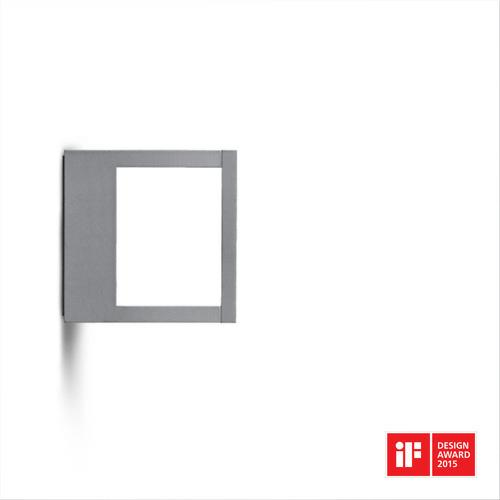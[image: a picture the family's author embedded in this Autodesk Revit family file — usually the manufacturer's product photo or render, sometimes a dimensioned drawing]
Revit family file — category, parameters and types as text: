
# Revit family: SIMES_S.7281W_Cool Square applique
name_source: partatom
category: Lighting Fixtures
revit_build: Autodesk Revit 2016 (Build: 20150714_1515(x64)
units: mm (PartAtom-declared; Revit-internal decimal feet)

## family parameters
Cut with Voids When Loaded = No
Host = Face
Light Source = Yes
OmniClass Number = 23.80.70.14
OmniClass Title = Luminaries for External Lighting
Part Type = Normal
Room Calculation Point = No
Round Connector Dimension = Use Diameter
Shared = No

## types (1)
- SIMES_S.7281W_Cool Square applique
    Approval mark = CE, ENEC
    Assembly Code = D5020
    Color Filter = 16777215
    Color Rendering Index = CRI 90
    Colour Temperature = 3000
    Control Gear = electronic transformer
    Default Elevation = 1219 mm
    Description = MINICOOL SQUARE APPLIQUE
Art. S.7281W
MODULES LED 3000K  230V CRI 90 MacAdam step 3
Rated luminaire luminous flux: 483lm
Rated input power: 12.5W
Luminaire efficacy: 39lm/W
Electronic ballast 220÷240V 0/50/60Hz
CE - ENEC 03

PRODUCT TYPE
Wall mounted luminaire or Bollard fitting ( bollard version ). IP rating IP 54
MATERIAL CHARACTERISTICS
Aluminium die cast housing in EN AB-47100 (low copper content) with high resistance against corrosion. Extruded EN AW-6060 aluminium structure (bollard version) with high corrosion resistance. Stone wash surface treatment prior to painting process. A4 grade Stainless Steel screws with 2,5-3% molybdenum content which increases the resistance against corrosion. Silicone gaskets. Painting Process : 3 Step Process
1) Surface treatment with BONDERITE. A heavy metal free chemical surface treatment containing ceramic nano particles giving a cohesive, inorganic and highly dense protective coating. 2) PRE POLYMERIZATION a process of introducing an epoxy primer with excellent characteristics to the paint which also offers very high resistance to oxidation due to its Zinc content. 3) POLYMERIZATION a process with the application of polyester powder with high resistance against UV rays and harsh weather conditions. Resistance test protection for Marine applications for 1200h.  Mechanical resistance IK 06
LIGHTING PERFORMANCE
Toughened glass diffuser. LOR --. Colour rendering index  CRI 90, Colour stability step  MacAdam step 3. 
WIRING
MICROCOOL hard wired with H07RN-F cable . MINICOOL and COOL is supplied with single cable entry.  Isolation: CLASS I . Available colours: White (cod.01), Aluminium grey (cod.14). Weight: 1.52 Kg Glow Wire test: --
Lamp included.
LOOK and COOL REGISTERED DESIGN
This luminaire contains built-in LED modules with energy class: A, A+, A++. In case of damage or malfunction please contact the manufacturer to receive additional instructions on how to replace and relative spare parts to order. The LED modules cannot be handled in the luminaire by the end user (Regulation UE 874/2012).
LED circuit boards are engineered accordingly to actual Lumen Maintenance regulation (LM80) and Technical Memorandum (TM21) where uniformity and quality of light is 50.000 hours referred to L70  B20 Ta 25°C.Lifecycle refers to LED circuit boards only, all others components of the luminaire are excluded.

EMERGENCY VERSIONS The fittings operates both on AC ( 50/60Hz ) and DC ( 0Hz ) voltage.
    Dimming Lamp Color Temperature Shift = <None>
    Frequency = 0/50/60Hz
    IFC Classification = Light Fixture
    IK Rating = IK 06
    Lamp = LED
    Lamp Light Flux = 1090
    Lamp count = 1
    Last Update = 02/08/2018 10:13:56
    Lifetime = 50000 L70 B20 Ta 25°C
    Light Output Ratio = 100
    Luminous efficacy = 38,6
    Manufacturer = SIMES
    Masterformat 2014 Code = 26 56 00
    Masterformat 2014 Description = Exterior Lighting
    Model = S.7281W
    Mounting Place = Wall
    Mounting Type = Surface mounted
    NBS Reference Code = 49
    NBS Reference Description = Luminaries And Lamps
    OmniClass Code = 23-35 47 11
    OmniClass Description = Lighting Fixture
    Photometric Web File = S7281W.ies
    Product Group = wall-mounted luminaire
    Product Name = Cool Square applique
    Protection Class = Protection class I
    Protection Degree = IP 54
    System Light Flux = 483
    System Power = 12,5
    Tilt Angle = 90.00°
    Type Comments = SIMES S.p.A. - All rights reserved
    Type Image = minicool_applique_quadrato.jpg
    UNSPSC Code = 3911
    URL = http://www.simes.it
    Uniclass 1.4 Code = YJ73
    Uniclass 1.4 Description = Luminaries and lamps
    Uniclass 2.0 Code = PR-49
    Uniclass 2.0 Description = Luminaries and lamps
    Uniclass 2015 Code = EF_70_80
    Uniclass 2015 Name = Lighting
    Uniformat II Code = D5020
    Uniformat II Description = Lighting & Branch Wiring
    Voltage = 220÷240V

## geometry (parser evidence)
native form markers: Sweep x1
no freeform markers — native parametric forms only
